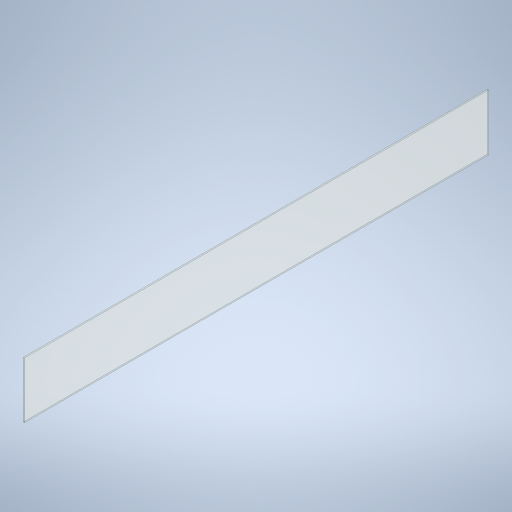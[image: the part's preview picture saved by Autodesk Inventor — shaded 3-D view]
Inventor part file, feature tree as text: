
AUTODESK INVENTOR PART (.ipt)
format: ipt  version: 2024 (Build 280153000, 153)  size: 235,520 bytes
history: native  units: in
note: dims shown in document units (in); Inventor stores cm internally (conversion verified against a paired STEP export)
features: extrude x1, sketch x1
ambient origin geometry x8: Origin, YZ Plane, XZ Plane, XY Plane, X Axis, Y Axis, Z Axis, Center Point
bodies: Solid1 (feature_tree)
feature tree (2):
  extrude  "Extrusion1"  Depth=291.5in
  sketch  "Sketch1"  dims[d2=35.25in d3=291.5in d4=0.75in d5=0.0in]
